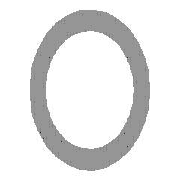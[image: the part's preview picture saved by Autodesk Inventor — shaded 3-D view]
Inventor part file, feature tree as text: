
AUTODESK INVENTOR PART (.ipt)
format: ipt  version: 2021 (Build 250183000, 183)  size: 206,848 bytes
history: native  units: mm (DEFAULTED — no unit token found)
features: other x5, plane x2, sketch x2, sweep x1
ambient origin geometry x8: Origin, YZ Plane, XZ Plane, XY Plane, X Axis, Y Axis, Z Axis, Center Point
bodies: Solid1 (feature_tree)
feature tree (10):
  parser-record x1  (decoder bookkeeping rows leaked as tree rows — omitted from the tree; the rows remain in map.json)
  other  "Driven Length"
  other  "Plano inicial"
  other  "Plano final"
  other  "Trayectoria de barrido"
  plane  "Plano de trabajo de orientación"
  sweep  "Cuerpo"
  sketch  "Sketch3"  dims[d0=21.336mm d1=3.7338mm]
  plane  "Work Plane3"
  sketch  "Sketch4"  dims[d4=-0.0mm d5=575.800269mm d6=90.0deg d7=575.800269mm d8=0.0mm d9=0.0mm]
